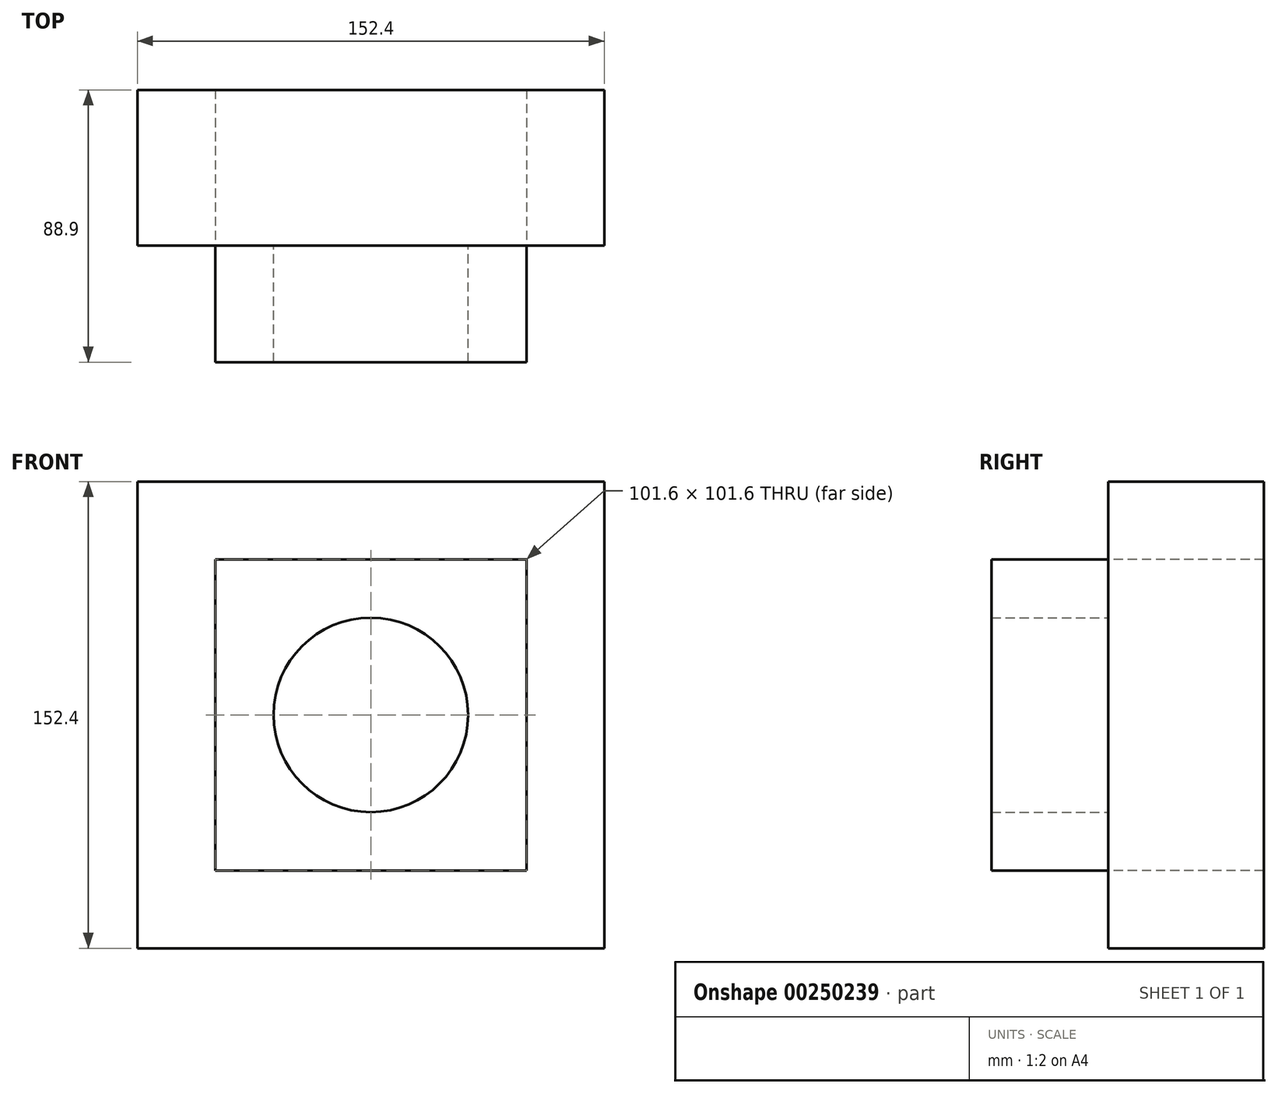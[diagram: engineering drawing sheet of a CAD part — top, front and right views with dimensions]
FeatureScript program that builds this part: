
annotation { "Feature Type Name" : "Feature", "Feature Type Description" : "" }
export const myFeature = defineFeature(function(context is Context, id is Id, definition is map)
    precondition{}
    {
        {
            var Q0;
            Q0=qCreatedBy(makeId("Front.planeOp"),FACE);
            var sketch = newSketch(context, id + "F0", { "sketchPlane" : qUnion([Q0])});
            skCircle(sketch, "E0", {"center": v(0, 0) * mm, "radius": 31.75 * mm});
            skLineSegment(sketch, "E1.bottom", {"start": v(50.8, 50.8) * mm, "end": v(-50.8, 50.8) * mm});
            skLineSegment(sketch, "E1.top", {"start": v(50.8, -50.8) * mm, "end": v(-50.8, -50.8) * mm});
            skLineSegment(sketch, "E1.left", {"start": v(50.8, 50.8) * mm, "end": v(50.8, -50.8) * mm});
            skLineSegment(sketch, "E1.right", {"start": v(-50.8, 50.8) * mm, "end": v(-50.8, -50.8) * mm});
            skLineSegment(sketch, "E2.bottom", {"start": v(76.2, 76.2) * mm, "end": v(-76.2, 76.2) * mm});
            skLineSegment(sketch, "E2.top", {"start": v(76.2, -76.2) * mm, "end": v(-76.2, -76.2) * mm});
            skLineSegment(sketch, "E2.left", {"start": v(76.2, 76.2) * mm, "end": v(76.2, -76.2) * mm});
            skLineSegment(sketch, "E2.right", {"start": v(-76.2, 76.2) * mm, "end": v(-76.2, -76.2) * mm});
            skSolve(sketch);
        }
        {
            var Q0;
            Q0=makeQuery(id+"F0.imprint","IMPRINT",FACE,{"disambiguationData":[TD([[makeQuery(id+"F0.imprint","IMPRINT",EDGE,{"derivedFrom":sQuery(id+"F0.wireOp",EDGE,"E0")}),-1.0]])]});
            extrude(context, id + "F1", {"entities" : qUnion([Q0]), "depth" : 38.1 * mm});
        }
        {
            var Q0;
            Q0=makeQuery(id+"F0.imprint","IMPRINT",FACE,{"disambiguationData":[TD([[makeQuery(id+"F0.imprint","IMPRINT",EDGE,{"derivedFrom":sQuery(id+"F0.wireOp",EDGE,"E1.bottom")}),-1.0]])]});
            extrude(context, id + "F2", {"entities" : qUnion([Q0]), "oppositeDirection" : true, "depth" : 50.8 * mm});
        }
    });
